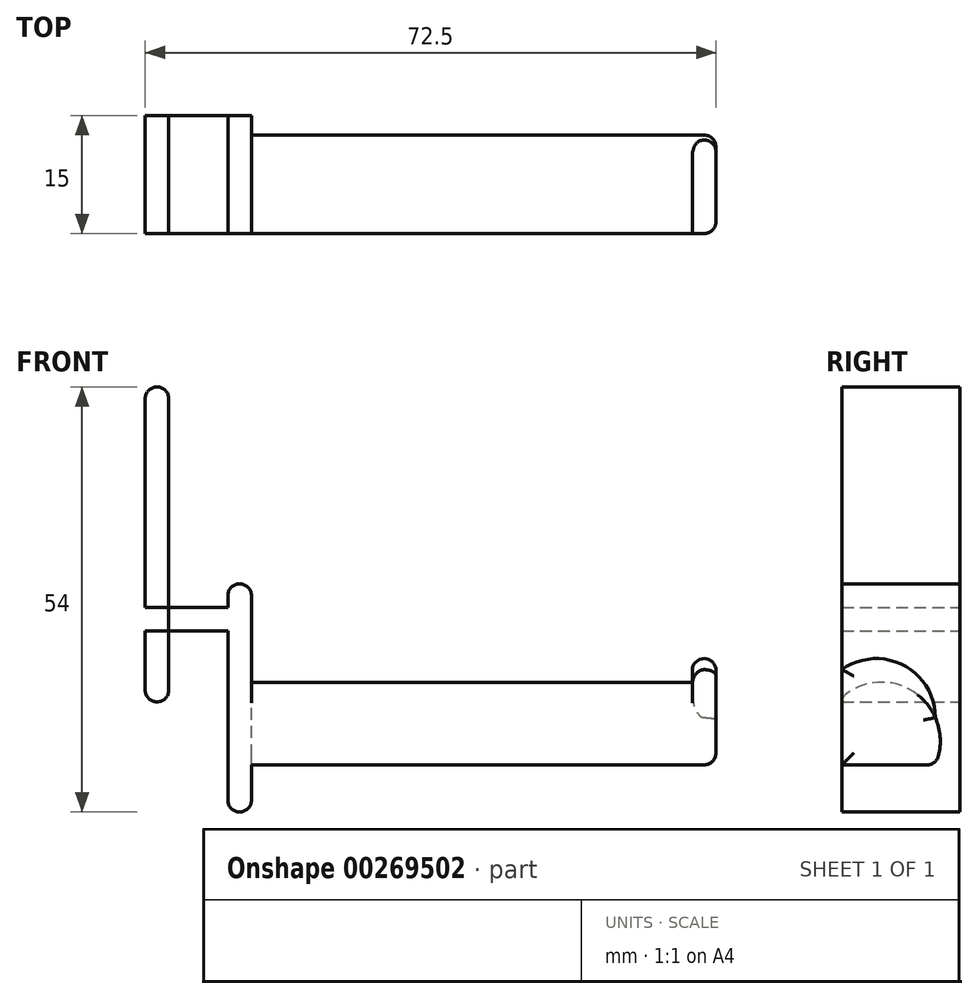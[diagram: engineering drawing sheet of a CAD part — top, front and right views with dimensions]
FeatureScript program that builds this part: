
annotation { "Feature Type Name" : "Feature", "Feature Type Description" : "" }
export const myFeature = defineFeature(function(context is Context, id is Id, definition is map)
    precondition{}
    {
        {
            var Q0;
            Q0=qCreatedBy(makeId("Front.planeOp"),FACE);
            var sketch = newSketch(context, id + "F0", { "sketchPlane" : qUnion([Q0])});
            skLineSegment(sketch, "E0.bottom", {"start": v(-23.5, 31) * mm, "end": v(-20.5, 31) * mm});
            skLineSegment(sketch, "E0.top", {"start": v(-23.5, -9) * mm, "end": v(-20.5, -9) * mm});
            skLineSegment(sketch, "E0.left", {"start": v(-23.5, 31) * mm, "end": v(-23.5, -9) * mm});
            skLineSegment(sketch, "E0.right", {"start": v(-20.5, 31) * mm, "end": v(-20.5, -9) * mm});
            skLineSegment(sketch, "E1.bottom", {"start": v(-23.5, 3) * mm, "end": v(-10, 3) * mm});
            skLineSegment(sketch, "E1.top", {"start": v(-23.5, 0) * mm, "end": v(-10, 0) * mm});
            skLineSegment(sketch, "E1.left", {"start": v(-23.5, 3) * mm, "end": v(-23.5, 0) * mm});
            skLineSegment(sketch, "E1.right", {"start": v(-10, 3) * mm, "end": v(-10, 0) * mm});
            skLineSegment(sketch, "E2.bottom", {"start": v(-10, 6) * mm, "end": v(-13, 6) * mm});
            skLineSegment(sketch, "E2.top", {"start": v(-10, -23) * mm, "end": v(-13, -23) * mm});
            skLineSegment(sketch, "E2.left", {"start": v(-10, 6) * mm, "end": v(-10, -23) * mm});
            skLineSegment(sketch, "E2.right", {"start": v(-13, 6) * mm, "end": v(-13, -23) * mm});
            skLineSegment(sketch, "E3", {"start": v(-10, 0) * mm, "end": v(0, 0) * mm, "construction": true});
            skSolve(sketch);
        }
        {
            var Q0;
            {var subQ0=sQuery(id+"F0.wireOp",EDGE,"E0.bottom");Q0=makeQuery(id+"F0.imprint","IMPRINT",FACE,{"disambiguationData":[TD([[makeQuery(id+"F0.imprint","IMPRINT",EDGE,{"derivedFrom":subQ0}),-1.0]])]});}
            var Q1;
            {var subQ0=sQuery(id+"F0.wireOp",EDGE,"E1.bottom");var subQ1=sQuery(id+"F0.wireOp",EDGE,"E0.right");var subQ2=makeQuery(id+"F0.imprint","INTERSECT",VERTEX,{"derivedFrom":[subQ1,subQ0]});Q1=makeQuery(id+"F0.imprint","IMPRINT",FACE,{"disambiguationData":[TD([[makeQuery(id+"F0.imprint","IMPRINT",EDGE,{"disambiguationData":[TD([[subQ2,-1.0]])],"derivedFrom":subQ1}),1.0]])]});}
            var Q2;
            {var subQ5=sQuery(id+"F0.wireOp",EDGE,"E1.left");Q2=makeQuery(id+"F0.imprint","IMPRINT",FACE,{"disambiguationData":[TD([[makeQuery(id+"F0.imprint","IMPRINT",EDGE,{"derivedFrom":subQ5}),1.0]])]});}
            var Q3;
            {var subQ0=sQuery(id+"F0.wireOp",EDGE,"E0.top");Q3=makeQuery(id+"F0.imprint","IMPRINT",FACE,{"disambiguationData":[TD([[makeQuery(id+"F0.imprint","IMPRINT",EDGE,{"derivedFrom":subQ0}),1.0]])]});}
            var Q4;
            {var subQ0=sQuery(id+"F0.wireOp",EDGE,"E2.left");var subQ1=sQuery(id+"F0.wireOp",EDGE,"E1.bottom");var subQ2=makeQuery(id+"F0.imprint","INTERSECT",VERTEX,{"derivedFrom":[subQ1,subQ0]});Q4=makeQuery(id+"F0.imprint","IMPRINT",FACE,{"disambiguationData":[TD([[makeQuery(id+"F0.imprint","IMPRINT",EDGE,{"disambiguationData":[TD([[subQ2,1.0]])],"derivedFrom":subQ1}),-1.0]])]});}
            var Q5;
            {var subQ5=sQuery(id+"F0.wireOp",EDGE,"E2.bottom");Q5=makeQuery(id+"F0.imprint","IMPRINT",FACE,{"disambiguationData":[TD([[makeQuery(id+"F0.imprint","IMPRINT",EDGE,{"derivedFrom":subQ5}),1.0]])]});}
            var Q6;
            {var subQ5=sQuery(id+"F0.wireOp",EDGE,"E2.top");Q6=makeQuery(id+"F0.imprint","IMPRINT",FACE,{"disambiguationData":[TD([[makeQuery(id+"F0.imprint","IMPRINT",EDGE,{"derivedFrom":subQ5}),-1.0]])]});}
            extrude(context, id + "F1", {"entities" : qUnion([Q0, Q1, Q2, Q3, Q4, Q5, Q6]), "depth" : 15 * mm});
        }
        {
            var Q0;
            Q0=makeQuery(id+"F1.opExtrude","SWEPT_FACE",FACE,{"disambiguationData":[OSD([sQuery(id+"F0.wireOp",EDGE,"E2.left")])]});
            var sketch = newSketch(context, id + "F2", { "sketchPlane" : qUnion([Q0])});
            skLineSegment(sketch, "E4", {"start": v(-15, 6) * mm, "end": v(-15, -23) * mm});
            skLineSegment(sketch, "E5", {"start": v(-15, -23) * mm, "end": v(0, -23) * mm, "construction": true});
            skLineSegment(sketch, "E6", {"start": v(0, -23) * mm, "end": v(0, 6) * mm, "construction": true});
            skLineSegment(sketch, "E7", {"start": v(0, 6) * mm, "end": v(-15, 6) * mm, "construction": true});
            skLineSegment(sketch, "E8", {"start": v(-15, -14) * mm, "end": v(0, -14) * mm, "construction": true});
            skCircle(sketch, "E9", {"center": v(-10, -14) * mm, "radius": 7.5 * mm});
            skLineSegment(sketch, "E10", {"start": v(-15, -17) * mm, "end": v(0, -17) * mm});
            skSolve(sketch);
        }
        {
            var Q0;
            {var subQ0=sQuery(id+"F2.wireOp",EDGE,"E10");var subQ1=sQuery(id+"F2.wireOp",EDGE,"E4");var subQ2=makeQuery(id+"F2.imprint","INTERSECT",VERTEX,{"derivedFrom":[subQ1,subQ0]});Q0=makeQuery(id+"F2.imprint","IMPRINT",FACE,{"disambiguationData":[TD([[makeQuery(id+"F2.imprint","IMPRINT",EDGE,{"disambiguationData":[TD([[subQ2,1.0]])],"derivedFrom":subQ1}),1.0]])]});}
            extrude(context, id + "F3", {"entities" : qUnion([Q0]), "operationType" : NewBodyOperationType.ADD, "depth" : 56 * mm});
        }
        {
            var Q0;
            Q0=makeQuery(id+"F3.opExtrude","CAP_FACE",FACE,{"disambiguationData":[OSD([sQuery(id+"F2.wireOp",EDGE,"E4"),sQuery(id+"F2.wireOp",EDGE,"E9"),sQuery(id+"F2.wireOp",EDGE,"E10")])],"isStart":false});
            var sketch = newSketch(context, id + "F4", { "sketchPlane" : qUnion([Q0])});
            skLineSegment(sketch, "E11", {"start": v(-15, -8.4) * mm, "end": v(-15, -17) * mm, "construction": true});
            skLineSegment(sketch, "E12", {"start": v(-15, -17) * mm, "end": v(-3.13, -17) * mm, "construction": true});
            skLineSegment(sketch, "E13", {"start": v(-10.63, -17) * mm, "end": v(-10.63, -11) * mm, "construction": true});
            skCircle(sketch, "E14", {"center": v(-10.63, -11) * mm, "radius": 7.5 * mm});
            skLineSegment(sketch, "E15", {"start": v(-15, -17) * mm, "end": v(-15, -1) * mm});
            skSolve(sketch);
        }
        {
            var Q0;
            {var subQ0=sQuery(id+"F4.wireOp",EDGE,"E15");var subQ1=sQuery(id+"F4.wireOp",EDGE,"E14");var subQ2=makeQuery(id+"F4.imprint","INTERSECT",VERTEX,{"derivedFrom":[subQ1,subQ0]});Q0=makeQuery(id+"F4.imprint","IMPRINT",FACE,{"disambiguationData":[TD([[makeQuery(id+"F4.imprint","IMPRINT",EDGE,{"disambiguationData":[TD([[subQ2,1.0]])],"derivedFrom":subQ1}),1.0]])]});}
            var Q1;
            {var subQ0=sQuery(id+"F4.wireOp",EDGE,"E14");var subQ1=makeQuery(id+"F3.opExtrude","CAP_EDGE",EDGE,{"disambiguationData":[OSD([sQuery(id+"F2.wireOp",EDGE,"E9")])],"isStart":false});var subQ2=makeQuery(id+"F4.imprint","INTERSECT",VERTEX,{"derivedFrom":[subQ1,subQ0]});Q1=makeQuery(id+"F4.imprint","IMPRINT",FACE,{"disambiguationData":[TD([[makeQuery(id+"F4.imprint","IMPRINT",EDGE,{"disambiguationData":[TD([[subQ2,1.0]])],"derivedFrom":subQ0}),1.0]])]});}
            var Q2;
            {var subQ0=sQuery(id+"F4.wireOp",EDGE,"E14");var subQ1=makeQuery(id+"F3.opExtrude","CAP_EDGE",EDGE,{"disambiguationData":[OSD([sQuery(id+"F2.wireOp",EDGE,"E9")])],"isStart":false});var subQ2=makeQuery(id+"F4.imprint","INTERSECT",VERTEX,{"derivedFrom":[subQ1,subQ0]});Q2=makeQuery(id+"F4.imprint","IMPRINT",FACE,{"disambiguationData":[TD([[makeQuery(id+"F4.imprint","IMPRINT",EDGE,{"disambiguationData":[TD([[subQ2,1.0]])],"derivedFrom":subQ0}),-1.0]])]});}
            extrude(context, id + "F5", {"entities" : qUnion([Q0, Q1, Q2]), "operationType" : NewBodyOperationType.ADD, "depth" : 3 * mm});
        }
        {
            var Q0;
            Q0=makeQuery(id+"F1.opExtrude","SWEPT_EDGE",EDGE,{"disambiguationData":[OSD([sQuery(id+"F0.wireOp",EDGE,"E2.bottom"),sQuery(id+"F0.wireOp",EDGE,"E2.left")])]});
            var Q1;
            Q1=makeQuery(id+"F1.opExtrude","SWEPT_EDGE",EDGE,{"disambiguationData":[OSD([sQuery(id+"F0.wireOp",EDGE,"E2.bottom"),sQuery(id+"F0.wireOp",EDGE,"E2.right")])]});
            var Q2;
            Q2=makeQuery(id+"F1.opExtrude","SWEPT_EDGE",EDGE,{"disambiguationData":[OSD([sQuery(id+"F0.wireOp",EDGE,"E0.bottom"),sQuery(id+"F0.wireOp",EDGE,"E0.right")])]});
            var Q3;
            Q3=makeQuery(id+"F1.opExtrude","SWEPT_EDGE",EDGE,{"disambiguationData":[OSD([sQuery(id+"F0.wireOp",EDGE,"E0.bottom"),sQuery(id+"F0.wireOp",EDGE,"E0.left")])]});
            var Q4;
            Q4=makeQuery(id+"F1.opExtrude","SWEPT_EDGE",EDGE,{"disambiguationData":[OSD([sQuery(id+"F0.wireOp",EDGE,"E0.top"),sQuery(id+"F0.wireOp",EDGE,"E0.left")])]});
            var Q5;
            Q5=makeQuery(id+"F1.opExtrude","SWEPT_EDGE",EDGE,{"disambiguationData":[OSD([sQuery(id+"F0.wireOp",EDGE,"E0.top"),sQuery(id+"F0.wireOp",EDGE,"E0.right")])]});
            var Q6;
            Q6=makeQuery(id+"F1.opExtrude","SWEPT_EDGE",EDGE,{"disambiguationData":[OSD([sQuery(id+"F0.wireOp",EDGE,"E2.top"),sQuery(id+"F0.wireOp",EDGE,"E2.left")])]});
            var Q7;
            Q7=makeQuery(id+"F1.opExtrude","SWEPT_EDGE",EDGE,{"disambiguationData":[OSD([sQuery(id+"F0.wireOp",EDGE,"E2.top"),sQuery(id+"F0.wireOp",EDGE,"E2.right")])]});
            var Q8;
            Q8=makeQuery(id+"F5.opExtrude","CAP_EDGE",EDGE,{"disambiguationData":[OSD([sQuery(id+"F4.wireOp",EDGE,"E14")])],"isStart":false});
            var Q9;
            Q9=makeQuery(id+"F5.opExtrude","CAP_EDGE",EDGE,{"disambiguationData":[OSD([sQuery(id+"F2.wireOp",EDGE,"E9")])],"isStart":false});
            var Q10;
            Q10=makeQuery(id+"F5.opExtrude","CAP_EDGE",EDGE,{"disambiguationData":[OSD([sQuery(id+"F2.wireOp",EDGE,"E10")])],"isStart":false});
            var Q11;
            Q11=makeQuery(id+"F5.opExtrude","CAP_EDGE",EDGE,{"disambiguationData":[OSD([sQuery(id+"F4.wireOp",EDGE,"E15")])],"isStart":false});
            var Q12;
            Q12=makeQuery(id+"F5.opExtrude","CAP_EDGE",EDGE,{"disambiguationData":[OSD([sQuery(id+"F4.wireOp",EDGE,"E14")])],"isStart":true});
            var Q13;
            {var subQ0=sQuery(id+"F2.wireOp",EDGE,"E10");var subQ1=sQuery(id+"F2.wireOp",EDGE,"E9");Q13=makeQuery(id+"F5.boolean.opBoolean","MERGE",EDGE,{"derivedFrom":[makeQuery(id+"F3.opExtrude","SWEPT_EDGE",EDGE,{"disambiguationData":[OSD([subQ1,subQ0])]}),makeQuery(id+"F5.opExtrude","SWEPT_EDGE",EDGE,{"disambiguationData":[OSD([subQ1,subQ0])]})]});}
            var Q14;
            Q14=makeQuery(id+"F3.opExtrude","SWEPT_EDGE",EDGE,{"disambiguationData":[OSD([sQuery(id+"F2.wireOp",EDGE,"E4"),sQuery(id+"F2.wireOp",EDGE,"E9")])]});
            fillet(context, id + "F6", {"entities" : qUnion([Q0, Q1, Q2, Q3, Q4, Q5, Q6, Q7, Q8, Q9, Q10, Q11, Q12, Q13, Q14]), "radius" : 1.5 * mm, "tangentPropagation" : true, "allowEdgeOverflow" : false});
        }
    });
